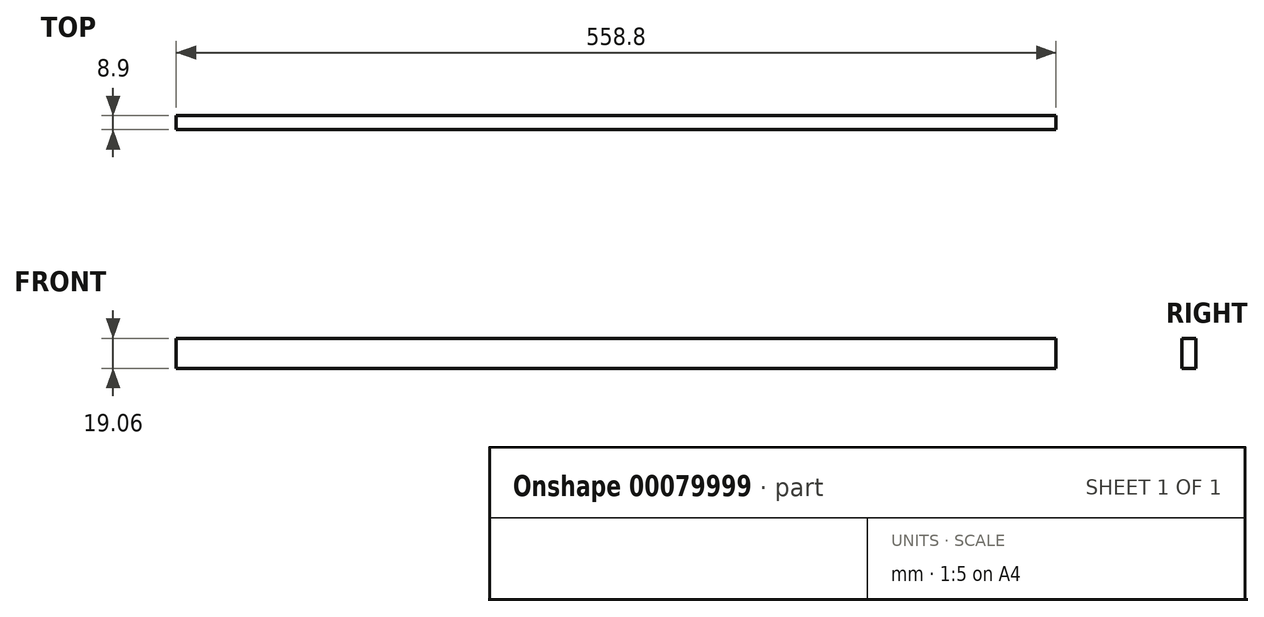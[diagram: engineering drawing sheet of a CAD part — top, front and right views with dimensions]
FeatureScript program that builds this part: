
annotation { "Feature Type Name" : "Feature", "Feature Type Description" : "" }
export const myFeature = defineFeature(function(context is Context, id is Id, definition is map)
    precondition{}
    {
        {
            var Q0;
            Q0=qCreatedBy(makeId("Front.planeOp"),FACE);
            var sketch = newSketch(context, id + "F0", { "sketchPlane" : qUnion([Q0])});
            skLineSegment(sketch, "E0.bottom", {"start": v(279.4, -9.52) * mm, "end": v(-279.4, -9.52) * mm});
            skLineSegment(sketch, "E0.top", {"start": v(279.4, 9.53) * mm, "end": v(-279.4, 9.52) * mm});
            skLineSegment(sketch, "E0.left", {"start": v(279.4, -9.52) * mm, "end": v(279.4, 9.53) * mm});
            skLineSegment(sketch, "E0.right", {"start": v(-279.4, -9.52) * mm, "end": v(-279.4, 9.53) * mm});
            skPoint(sketch, "E0.middle", {"position": v(0, 0) * mm});
            skSolve(sketch);
        }
        {
            var Q0;
            Q0=makeQuery(id+"F0.imprint","IMPRINT",FACE,{"disambiguationData":[TD([[makeQuery(id+"F0.imprint","IMPRINT",EDGE,{"derivedFrom":sQuery(id+"F0.wireOp",EDGE,"E0.bottom")}),-1.0]])]});
            extrude(context, id + "F1", {"entities" : qUnion([Q0]), "endBound" : BoundingType.SYMMETRIC, "depth" : 8.9 * mm});
        }
    });
